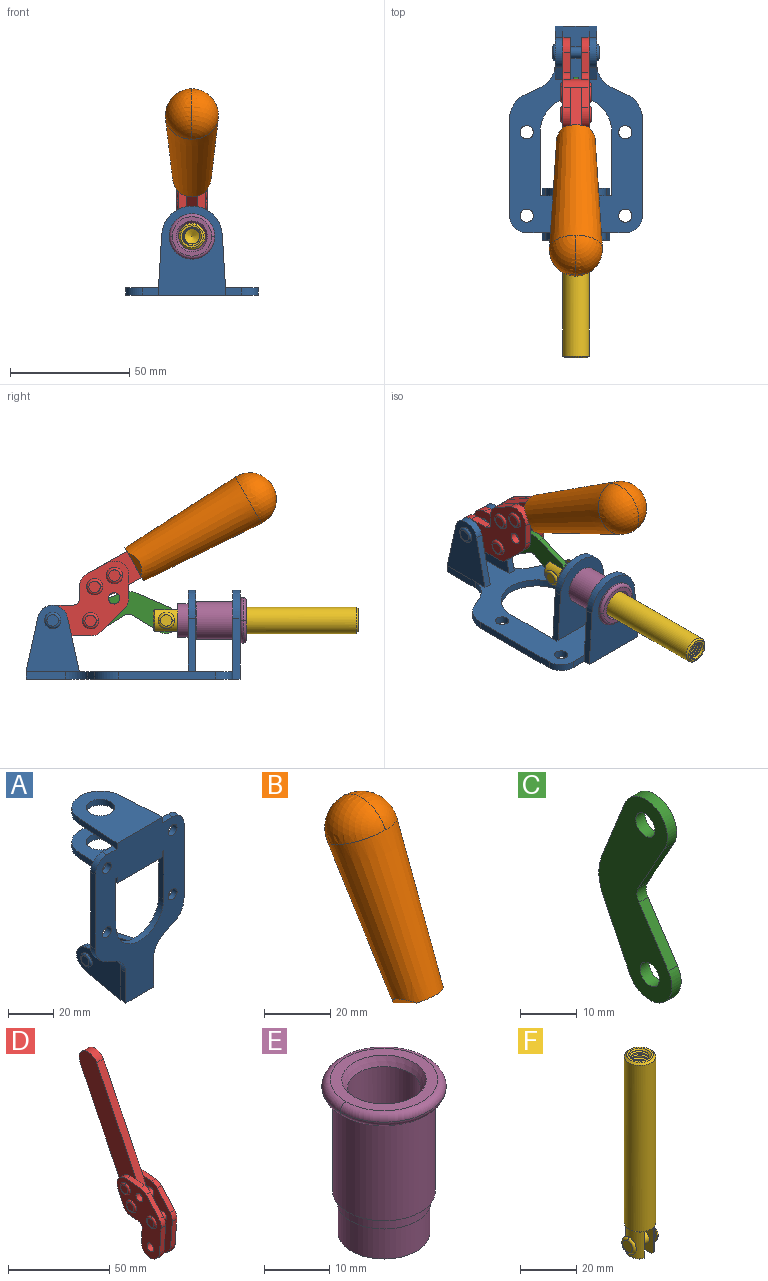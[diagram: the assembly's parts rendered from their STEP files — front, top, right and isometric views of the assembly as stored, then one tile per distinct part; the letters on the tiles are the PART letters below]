
ASSEMBLY  parts=6 mates=6
PART A: 55 faces, bbox 55.7x37.4x89.8 mm
  f0: torus R=2.41mm, axis (-1,0,0), area 15mm2, adj f11,f15,f25
  f1: torus R=2.41mm, axis (-1,0,0), area 15mm2, adj f10,f12,f22
  f2: cylinder r=2.78mm len=5.56mm, axis (0,-1,0), area 54.2mm2, adj f30,f54
  f3: cylinder r=14.99mm len=29.97mm, axis (0,-1,0), area 145.9mm2, adj f30,f49,f53,f54
  f4: cylinder r=2.78mm len=5.56mm, axis (0,-1,0), area 54.2mm2, adj f30,f54
  f5: cylinder r=2.78mm len=5.56mm, axis (0,-1,0), area 54.2mm2, adj f30,f54
  f6: cylinder r=2.78mm len=5.56mm, axis (0,-1,0), area 54.2mm2, adj f30,f54
  f7: cylinder r=6.35mm len=12.7mm, axis (0,0,1), area 123.6mm2, adj f27,f51
  f8: cylinder r=6.35mm len=12.7mm, axis (0,0,-1), area 124.7mm2, adj f21,f35
  f9: cylinder r=2.41mm len=11.18mm, axis (-1,0,0), area 169.4mm2, adj f16,f19
  f10: plane 4.83x4.83mm, normal (1,0,0), area 18.3mm2, adj f1,f12
  f11: plane 4.83x4.83mm, normal (-1,0,0), area 18.3mm2, adj f0,f15
  f12: torus R=2.41mm, axis (-1,0,0), area 15mm2, adj f1,f10,f22
  f13: cylinder r=6.35mm len=12.41mm, axis (1,0,0), area 53.4mm2, adj f18,f19,f22,f23
  f14: cylinder r=6.35mm len=12.41mm, axis (-1,0,0), area 53.4mm2, adj f16,f17,f24,f25
  f15: torus R=2.41mm, axis (-1,0,0), area 15mm2, adj f0,f11,f25
  f16: plane 27.86x22.35mm, normal (1,0,0), area 425.4mm2, adj f9,f14,f17,f24,f30
  f17: plane 22.86x4.97mm, normal (0,0.21,0.98), area 72.5mm2, adj f14,f16,f25,f30
  f18: plane 22.86x4.97mm, normal (0,0.21,0.98), area 72.5mm2, adj f13,f19,f22,f30
  f19: plane 27.86x22.35mm, normal (-1,0,0), area 425.4mm2, adj f9,f13,f18,f23,f30
  f20: cylinder r=12.7mm len=25.35mm, axis (0,0,-1), area 119.8mm2, adj f21,f34,f35,f36
  f21: plane 34.21x28.07mm, normal (0,0,-1), area 702.4mm2, adj f8,f20,f30,f34,f36
  f22: plane 27.96x22.45mm, normal (1,0,0), area 407.2mm2, adj f1,f12,f13,f18,f23,f30,f42,f43
  f23: plane 22.86x4.97mm, normal (0,0.21,-0.98), area 72.5mm2, adj f13,f19,f22,f44
  f24: plane 22.86x4.97mm, normal (0,0.21,-0.98), area 72.5mm2, adj f14,f16,f25,f44
  f25: plane 27.86x22.35mm, normal (-1,0,0), area 407.1mm2, adj f0,f14,f15,f17,f24,f30,f45,f46
  f26: plane 3.1x0.95mm, normal (0,0,-1), area 2.7mm2, adj f30,f49,f50,f54
  f27: plane 34.21x28.07mm, normal (0,0,1), area 702.4mm2, adj f7,f28,f30,f50,f52
  f28: cylinder r=12.7mm len=25.35mm, axis (0,0,1), area 118.8mm2, adj f27,f50,f51,f52
  f29: plane 3.1x0.95mm, normal (0,0,-1), area 2.7mm2, adj f30,f52,f53,f54
  f30: plane 86.54x55.63mm, normal (0,1,0), area 2362.9mm2, adj f2,f3,f4,f5,f6,f16,f17,f18
  f31: plane 40.56x3.1mm, normal (-1,0,0), area 125.7mm2, adj f30,f32,f48,f54
  f32: cylinder r=7.11mm len=7.11mm, axis (0,-1,0), area 34.6mm2, adj f30,f31,f33,f54
  f33: plane 6.67x3.1mm, normal (0,0,1), area 20.4mm2, adj f30,f32,f34,f54
  f34: plane 25.39x3.13mm, normal (-1,0.06,0), area 79.5mm2, adj f20,f21,f33,f35,f54
  f35: plane 37.31x28.45mm, normal (0,0,1), area 789.9mm2, adj f8,f20,f34,f36,f54
  f36: plane 25.39x3.13mm, normal (1,0.06,0), area 79.5mm2, adj f20,f21,f35,f37,f54
  f37: plane 6.67x3.1mm, normal (0,0,1), area 20.4mm2, adj f30,f36,f38,f54
  f38: cylinder r=7.11mm len=7.11mm, axis (0,-1,0), area 34.6mm2, adj f30,f37,f39,f54
  f39: plane 40.56x3.1mm, normal (1,0,0), area 125.7mm2, adj f30,f38,f40,f54
  f40: cylinder r=11.18mm len=10.16mm, axis (0,-1,0), area 39.5mm2, adj f30,f39,f41,f54
  f41: plane 6.09x3.1mm, normal (0.42,0,-0.91), area 20.8mm2, adj f30,f40,f42,f54
  f42: cylinder r=11.18mm len=9.41mm, axis (0,-1,0), area 37.2mm2, adj f22,f30,f41,f43,f54
  f43: plane 16.5x3.1mm, normal (1,0,0), area 51.1mm2, adj f22,f42,f44,f54
  f44: plane 17.37x3.1mm, normal (0,0,-1), area 53.8mm2, adj f23,f24,f30,f43,f45,f54
  f45: plane 16.5x3.1mm, normal (-1,0,0), area 51.1mm2, adj f25,f44,f46,f54
  f46: cylinder r=11.18mm len=9.41mm, axis (0,-1,0), area 37.2mm2, adj f25,f30,f45,f47,f54
  f47: plane 6.09x3.1mm, normal (-0.42,0,-0.91), area 20.8mm2, adj f30,f46,f48,f54
  f48: cylinder r=11.18mm len=10.16mm, axis (0,-1,0), area 39.5mm2, adj f30,f31,f47,f54
  f49: plane 26.54x3.1mm, normal (-1,0,0), area 82.3mm2, adj f3,f26,f30,f54
  f50: plane 25.39x3.1mm, normal (1,0.06,0), area 78.8mm2, adj f26,f27,f28,f51,f54
  f51: plane 37.31x28.45mm, normal (0,0,-1), area 789.9mm2, adj f7,f28,f50,f52,f54
  f52: plane 25.39x3.1mm, normal (-1,0.06,0), area 78.8mm2, adj f27,f28,f29,f51,f54
  f53: plane 26.54x3.1mm, normal (1,0,0), area 82.3mm2, adj f3,f29,f30,f54
  f54: plane 89.66x55.63mm, normal (0,-1,0), area 2678.5mm2, adj f2,f3,f4,f5,f6,f26,f29,f31
PART B: 11 faces, bbox 22.3x42.6x64.5 mm
  f0: sphere r=11.13mm, area 411.4mm2, adj f1,f8
  f1: cone r=11.11mm half-angle=3.3deg, axis (0,0.44,0.9), area 3251.8mm2, adj f0,f7,f8,f9,f10
  f2: cylinder r=6.16mm len=11.7mm, axis (1,0,0), area 89.5mm2, adj f3,f4,f5,f6
  f3: plane 60.23x36.75mm, normal (-1,0,0), area 763.6mm2, adj f2,f4,f6,f10
  f4: plane 51.37x25.05mm, normal (0,0.9,-0.44), area 264.2mm2, adj f2,f3,f5,f10
  f5: plane 60.23x36.75mm, normal (1,0,0), area 763.6mm2, adj f2,f4,f6,f10
  f6: plane 51.37x25.05mm, normal (0,-0.9,0.44), area 264.2mm2, adj f2,f3,f5,f10
  f7: plane 9.95x5.95mm, normal (0.71,-0.31,-0.64), area 25.8mm2, adj f1,f10
  f8: sphere r=11.13mm, area 411.4mm2, adj f0,f1
  f9: plane 9.95x5.95mm, normal (-0.71,-0.31,-0.64), area 25.8mm2, adj f1,f10
  f10: plane 14.27x11.38mm, normal (0,-0.44,-0.9), area 106.7mm2, adj f1,f3,f4,f5,f6,f7,f9
PART C: 12 faces, bbox 2.3x18.2x42.8 mm
  f0: cylinder r=2.4mm len=4.8mm, axis (1,0,0), area 34.9mm2, adj f4,f11
  f1: cylinder r=10.41mm len=8.47mm, axis (1,0,0), area 20.2mm2, adj f4,f9,f10,f11
  f2: cylinder r=3.05mm len=3.16mm, axis (1,0,0), area 7.7mm2, adj f4,f6,f7,f11
  f3: cylinder r=2.4mm len=4.8mm, axis (1,0,0), area 34.9mm2, adj f4,f11
  f4: plane 42.81x18.23mm, normal (-1,0,0), area 414.1mm2, adj f0,f1,f2,f3,f5,f6,f7,f8
  f5: cylinder r=5.54mm len=10.67mm, axis (1,0,0), area 41.8mm2, adj f4,f6,f10,f11
  f6: plane 11.66x6.53mm, normal (0,-0.87,-0.49), area 30.9mm2, adj f2,f4,f5,f11
  f7: plane 11.17x7.33mm, normal (0,-0.84,0.55), area 30.9mm2, adj f2,f4,f8,f11
  f8: cylinder r=5.54mm len=10.51mm, axis (1,0,0), area 41.8mm2, adj f4,f7,f9,f11
  f9: plane 13.67x6.67mm, normal (0,0.9,-0.44), area 35.1mm2, adj f1,f4,f8,f11
  f10: plane 14.1x5.7mm, normal (0,0.93,0.37), area 35.1mm2, adj f1,f4,f5,f11
  f11: plane 42.81x18.23mm, normal (1,0,0), area 414.1mm2, adj f0,f1,f2,f3,f5,f6,f7,f8
PART D: 59 faces, bbox 12.9x60.2x99.6 mm
  f0: torus R=2.39mm, axis (-1,0,0), area 14.9mm2, adj f20,f43,f51
  f1: torus R=2.39mm, axis (-1,0,0), area 14.9mm2, adj f19,f42,f51
  f2: torus R=2.39mm, axis (-1,0,0), area 14.9mm2, adj f18,f35,f51
  f3: torus R=2.39mm, axis (-1,0,0), area 14.9mm2, adj f14,f17,f23
  f4: torus R=2.39mm, axis (-1,0,0), area 14.9mm2, adj f13,f16,f23
  f5: torus R=2.39mm, axis (-1,0,0), area 14.9mm2, adj f12,f15,f23
  f6: cylinder r=2.39mm len=4.78mm, axis (1,0,0), area 46.5mm2, adj f48,f50,f51
  f7: cylinder r=2.39mm len=4.78mm, axis (1,0,0), area 46.5mm2, adj f50,f51
  f8: cylinder r=6.35mm len=12.68mm, axis (1,0,0), area 61.8mm2, adj f38,f39,f50,f51
  f9: cylinder r=2.39mm len=4.78mm, axis (-1,0,0), area 70.5mm2, adj f46,f50
  f10: cylinder r=2.39mm len=4.78mm, axis (-1,0,0), area 46.5mm2, adj f23,f45,f46
  f11: cylinder r=2.39mm len=4.78mm, axis (-1,0,0), area 46.5mm2, adj f23,f46
  f12: plane 4.78x4.78mm, normal (1,0,0), area 17.9mm2, adj f5,f15
  f13: plane 4.78x4.78mm, normal (1,0,0), area 17.9mm2, adj f4,f16
  f14: plane 4.78x4.78mm, normal (1,0,0), area 17.9mm2, adj f3,f17
  f15: torus R=2.39mm, axis (-1,0,0), area 14.9mm2, adj f5,f12,f23
  f16: torus R=2.39mm, axis (-1,0,0), area 14.9mm2, adj f4,f13,f23
  f17: torus R=2.39mm, axis (-1,0,0), area 14.9mm2, adj f3,f14,f23
  f18: plane 4.78x4.78mm, normal (-1,0,0), area 17.9mm2, adj f2,f35
  f19: plane 4.78x4.78mm, normal (-1,0,0), area 17.9mm2, adj f1,f42
  f20: plane 4.78x4.78mm, normal (-1,0,0), area 17.9mm2, adj f0,f43
  f21: plane 2.26x0.2mm, normal (1,0,0), area 0.2mm2, adj f31,f44
  f22: plane 2.26x0.2mm, normal (-1,0,0), area 0.2mm2, adj f41,f44
  f23: plane 39.37x30.77mm, normal (1,0,0), area 565.5mm2, adj f3,f4,f5,f10,f11,f15,f16,f17
  f24: cylinder r=6.1mm len=4.15mm, axis (-1,0,0), area 14.7mm2, adj f23,f25,f32,f46
  f25: plane 10.25x9.01mm, normal (0,-0.75,0.66), area 42.3mm2, adj f23,f24,f26,f46
  f26: cylinder r=6.35mm len=4.64mm, axis (-1,0,0), area 15.6mm2, adj f23,f25,f27,f46
  f27: plane 15.84x3.1mm, normal (0,-1,-0.07), area 49.2mm2, adj f23,f26,f28,f46
  f28: cylinder r=6.35mm len=12.68mm, axis (-1,0,0), area 61.8mm2, adj f23,f27,f29,f46
  f29: plane 8.11x3.1mm, normal (0,1,0.07), area 25.2mm2, adj f23,f28,f30,f46
  f30: cylinder r=3.05mm len=3.25mm, axis (-1,0,0), area 14.8mm2, adj f23,f29,f31,f46
  f31: plane 5.99x3.1mm, normal (0,0.07,-1), area 18.6mm2, adj f21,f23,f30,f44,f46
  f32: plane 9.5x3.1mm, normal (0,-0.07,1), area 29.5mm2, adj f23,f24,f33,f46,f47
  f33: cylinder r=6.1mm len=8.63mm, axis (-1,0,0), area 39.1mm2, adj f23,f32,f34,f47
  f34: plane 8.65x3.96mm, normal (0,0.91,-0.42), area 29.5mm2, adj f23,f33,f44,f47
  f35: torus R=2.39mm, axis (-1,0,0), area 14.9mm2, adj f2,f18,f51
  f36: plane 10.25x9.01mm, normal (0,-0.75,0.66), area 42.3mm2, adj f37,f49,f50,f51
  f37: cylinder r=6.35mm len=4.64mm, axis (1,0,0), area 15.6mm2, adj f36,f38,f50,f51
  f38: plane 15.84x3.1mm, normal (0,-1,-0.07), area 49.2mm2, adj f8,f37,f50,f51
  f39: plane 8.11x3.1mm, normal (0,1,0.07), area 25.2mm2, adj f8,f40,f50,f51
  f40: cylinder r=3.05mm len=3.25mm, axis (1,0,0), area 14.8mm2, adj f39,f41,f50,f51
  f41: plane 5.99x3.1mm, normal (0,0.07,-1), area 18.6mm2, adj f22,f40,f44,f50,f51
  f42: torus R=2.39mm, axis (-1,0,0), area 14.9mm2, adj f1,f19,f51
  f43: torus R=2.39mm, axis (-1,0,0), area 14.9mm2, adj f0,f20,f51
  f44: cylinder r=6.35mm len=12.12mm, axis (-1,0,0), area 128.9mm2, adj f21,f22,f23,f31,f34,f41,f46,f47
  f45: plane 2.65x1.35mm, normal (1,0,0), area 1mm2, adj f10,f55
  f46: plane 39.08x20.42mm, normal (-1,0,0), area 412.5mm2, adj f9,f10,f11,f24,f25,f26,f27,f28
  f47: plane 77.62x39.82mm, normal (1,0,0), area 850mm2, adj f32,f33,f34,f44,f53,f54,f55
  f48: plane 2.65x1.35mm, normal (-1,0,0), area 1mm2, adj f6,f55
  f49: cylinder r=6.1mm len=4.15mm, axis (1,0,0), area 14.7mm2, adj f36,f50,f51,f56
  f50: plane 39.08x20.42mm, normal (1,0,0), area 412.5mm2, adj f6,f7,f8,f9,f36,f37,f38,f39
  f51: plane 39.37x30.77mm, normal (-1,0,0), area 565.5mm2, adj f0,f1,f2,f6,f7,f8,f35,f36
  f52: plane 8.65x3.96mm, normal (0,0.91,-0.42), area 29.5mm2, adj f44,f51,f57,f58
  f53: plane 68.49x33.4mm, normal (0,0.9,-0.44), area 358.1mm2, adj f44,f47,f54,f58
  f54: cylinder r=6.35mm len=12.06mm, axis (1,0,0), area 93.7mm2, adj f47,f53,f55,f58
  f55: plane 68.49x33.4mm, normal (0,-0.9,0.44), area 358.1mm2, adj f44,f45,f46,f47,f48,f50,f54,f58
  f56: plane 9.5x3.1mm, normal (0,-0.07,1), area 29.5mm2, adj f49,f50,f51,f57,f58
  f57: cylinder r=6.1mm len=8.63mm, axis (1,0,0), area 39.1mm2, adj f51,f52,f56,f58
  f58: plane 77.62x39.82mm, normal (-1,0,0), area 850mm2, adj f44,f52,f53,f54,f55,f56,f57
PART E: 15 faces, bbox 20.6x20.6x28.7 mm
  f0: torus R=8.26mm, axis (0,0,1), area 56.8mm2, adj f1,f10,f12
  f1: torus R=8.26mm, axis (0,0,1), area 56.8mm2, adj f0,f6,f13
  f2: cylinder r=5.59mm len=25.91mm, axis (0,0,1), area 909.6mm2, adj f3,f4
  f3: cone r=6.86mm half-angle=45deg, axis (0,0,-1), area 70.2mm2, adj f2,f14
  f4: cone r=6.47mm half-angle=30deg, axis (0,0,1), area 66.7mm2, adj f2,f13
  f5: cylinder r=7.04mm len=14.07mm, axis (0,0,1), area 252.6mm2, adj f11,f14
  f6: torus R=8.26mm, axis (0,0,1), area 56.8mm2, adj f1,f12,f13
  f7: cylinder r=7.16mm len=14.33mm, axis (0,0,1), area 91.5mm2, adj f9,f11
  f8: cylinder r=7.86mm len=18.42mm, axis (0,0,1), area 909.6mm2, adj f9,f10
  f9: plane 15.72x15.72mm, normal (0,0,-1), area 33mm2, adj f7,f8
  f10: plane 16.51x16.51mm, normal (0,0,-1), area 19.9mm2, adj f0,f8,f12
  f11: plane 14.33x14.33mm, normal (0,0,-1), area 5.7mm2, adj f5,f7
  f12: torus R=8.26mm, axis (0,0,1), area 56.8mm2, adj f0,f6,f10
  f13: plane 16.51x16.51mm, normal (0,0,1), area 82.7mm2, adj f1,f4,f6
  f14: plane 14.07x14.07mm, normal (0,0,-1), area 7.8mm2, adj f3,f5
PART F: 48 faces, bbox 12.6x11.1x86.1 mm
  f0: torus R=2.41mm, axis (-1,0,0), area 15mm2, adj f30,f32,f34
  f1: torus R=2.41mm, axis (-1,0,0), area 15mm2, adj f29,f31,f33
  f2: cylinder r=5.54mm len=72.39mm, axis (0,0,1), area 2518.5mm2, adj f3,f4,f42,f43
  f3: cone r=5.54mm half-angle=45deg, axis (0,0,1), area 7.6mm2, adj f2,f5,f41
  f4: cone r=5.54mm half-angle=45deg, axis (0,0,-1), area 34.9mm2, adj f2,f39
  f5: cylinder r=5.08mm len=11.48mm, axis (0,0,1), area 108.3mm2, adj f3,f7,f8,f41
  f6: cylinder r=2.41mm len=4.83mm, axis (-1,0,0), area 71.2mm2, adj f40,f41
  f7: cylinder r=2.41mm len=4.83mm, axis (-1,0,0), area 7.6mm2, adj f5,f34
  f8: cone r=5.08mm half-angle=45deg, axis (0,0,1), area 10.6mm2, adj f5,f37,f41
  f9: cone r=3.98mm half-angle=45deg, axis (0,0,1), area 17.6mm2, adj f27,f39,f45,f46,f47
  f10: cylinder r=2.41mm len=4.83mm, axis (-1,0,0), area 7.6mm2, adj f33,f38
  f11: cylinder r=3.2mm len=6.4mm, axis (0,0,1), area 78.4mm2, adj f12,f28,f44,f45,f47
  f12: cylinder r=3.2mm len=6.4mm, axis (0,0,1), area 10.5mm2, adj f11,f13,f45,f47
  f13: cylinder r=3.2mm len=6.4mm, axis (0,0,1), area 10.5mm2, adj f12,f14,f45,f47
  f14: cylinder r=3.2mm len=6.4mm, axis (0,0,1), area 10.5mm2, adj f13,f15,f45,f47
  f15: cylinder r=3.2mm len=6.4mm, axis (0,0,1), area 10.5mm2, adj f14,f16,f45,f47
  f16: cylinder r=3.2mm len=6.4mm, axis (0,0,1), area 10.5mm2, adj f15,f17,f45,f47
  f17: cylinder r=3.2mm len=6.4mm, axis (0,0,1), area 10.5mm2, adj f16,f18,f45,f47
  f18: cylinder r=3.2mm len=6.4mm, axis (0,0,1), area 10.5mm2, adj f17,f19,f45,f47
  f19: cylinder r=3.2mm len=6.4mm, axis (0,0,1), area 10.5mm2, adj f18,f20,f45,f47
  f20: cylinder r=3.2mm len=6.4mm, axis (0,0,1), area 10.5mm2, adj f19,f21,f45,f47
  f21: cylinder r=3.2mm len=6.4mm, axis (0,0,1), area 10.5mm2, adj f20,f22,f45,f47
  f22: cylinder r=3.2mm len=6.4mm, axis (0,0,1), area 10.5mm2, adj f21,f23,f45,f47
  f23: cylinder r=3.2mm len=6.4mm, axis (0,0,1), area 10.5mm2, adj f22,f24,f45,f47
  f24: cylinder r=3.2mm len=6.4mm, axis (0,0,1), area 10.5mm2, adj f23,f25,f45,f47
  f25: cylinder r=3.2mm len=6.4mm, axis (0,0,1), area 10.5mm2, adj f24,f26,f45,f47
  f26: cylinder r=3.2mm len=6.4mm, axis (0,0,1), area 10.5mm2, adj f25,f27,f45,f47
  f27: cylinder r=3.2mm len=6.4mm, axis (0,0,1), area 7.4mm2, adj f9,f26,f45,f47
  f28: cone r=3.2mm half-angle=60deg, axis (0,0,1), area 37.2mm2, adj f11
  f29: plane 4.83x4.83mm, normal (-1,0,0), area 18.3mm2, adj f1,f31
  f30: plane 4.83x4.83mm, normal (1,0,0), area 18.3mm2, adj f0,f32
  f31: torus R=2.41mm, axis (-1,0,0), area 15mm2, adj f1,f29,f33
  f32: torus R=2.41mm, axis (-1,0,0), area 15mm2, adj f0,f30,f34
  f33: plane 6.83x6.83mm, normal (1,0,0), area 18.3mm2, adj f1,f10,f31
  f34: plane 6.83x6.83mm, normal (-1,0,0), area 18.3mm2, adj f0,f7,f32
  f35: cone r=5.08mm half-angle=45deg, axis (0,0,1), area 10.6mm2, adj f36,f38,f40
  f36: plane 7.25x1.97mm, normal (0,0,-1), area 10mm2, adj f35,f40
  f37: plane 7.25x1.97mm, normal (0,0,-1), area 10mm2, adj f8,f41
  f38: cylinder r=5.08mm len=11.48mm, axis (0,0,1), area 108.3mm2, adj f10,f35,f40,f42
  f39: plane 9.55x9.55mm, normal (0,0,1), area 22mm2, adj f4,f9
  f40: plane 12.76x10.09mm, normal (1,0,0), area 95.7mm2, adj f6,f35,f36,f38,f42,f43
  f41: plane 12.76x10.09mm, normal (-1,0,0), area 95.7mm2, adj f3,f5,f6,f8,f37,f43
  f42: cone r=5.54mm half-angle=45deg, axis (0,0,1), area 7.6mm2, adj f2,f38,f40
  f43: plane 11.07x4.7mm, normal (0,0,-1), area 50.4mm2, adj f2,f40,f41
  f44: plane 0.89x0.62mm, normal (-1,0,0), area 0.3mm2, adj f11,f45,f46,f47
  f45: bspline ~24.8x7.63mm, area 266.6mm2, adj f9,f11,f12,f13,f14,f15,f16,f17
  f46: bspline ~24.87x7.63mm, area 73.6mm2, adj f9,f44,f45,f47
  f47: bspline ~24.98x7.63mm, area 272.5mm2, adj f9,f11,f12,f13,f14,f15,f16,f17
PLACE A rot(axis=(1,0,0),90deg) t=(0,9.43,0)mm fixed
PLACE B rot(axis=(1,0,0),86.6deg) t=(-0.04,8.04,1.93)mm
PLACE C rot(axis=(0,-0.72,-0.69),180deg) t=(0,9.19,0.47)mm
PLACE D rot(axis=(1,0,0),86.6deg) t=(0,8.04,1.93)mm
PLACE E rot(axis=(1,0,0),90deg) t=(0,9.43,0)mm
PLACE F rot(axis=(1,0,0),90deg) t=(0,9.37,0)mm
MATE revolute F.f6 <-> C.f3  axis (-1,0,0) through (0,-6.1,24.61)mm
MATE slider F.f2 <-> E.f2  axis (0,-1,0) through (0,-49.41,24.61)mm
MATE fastened E.f0 <-> A.f7  axis (0,1,0) through (0,-36.96,24.61)mm
MATE fastened D.f54 <-> B.f2  axis (-1,0,0) through (-2.35,-42.46,76.08)mm
MATE revolute D.f7 <-> A.f0  axis (-1,0,0) through (0,41.52,24.61)mm
MATE revolute C.f5 <-> D.f4  axis (-1,0,0) through (0,25.65,24.44)mm
